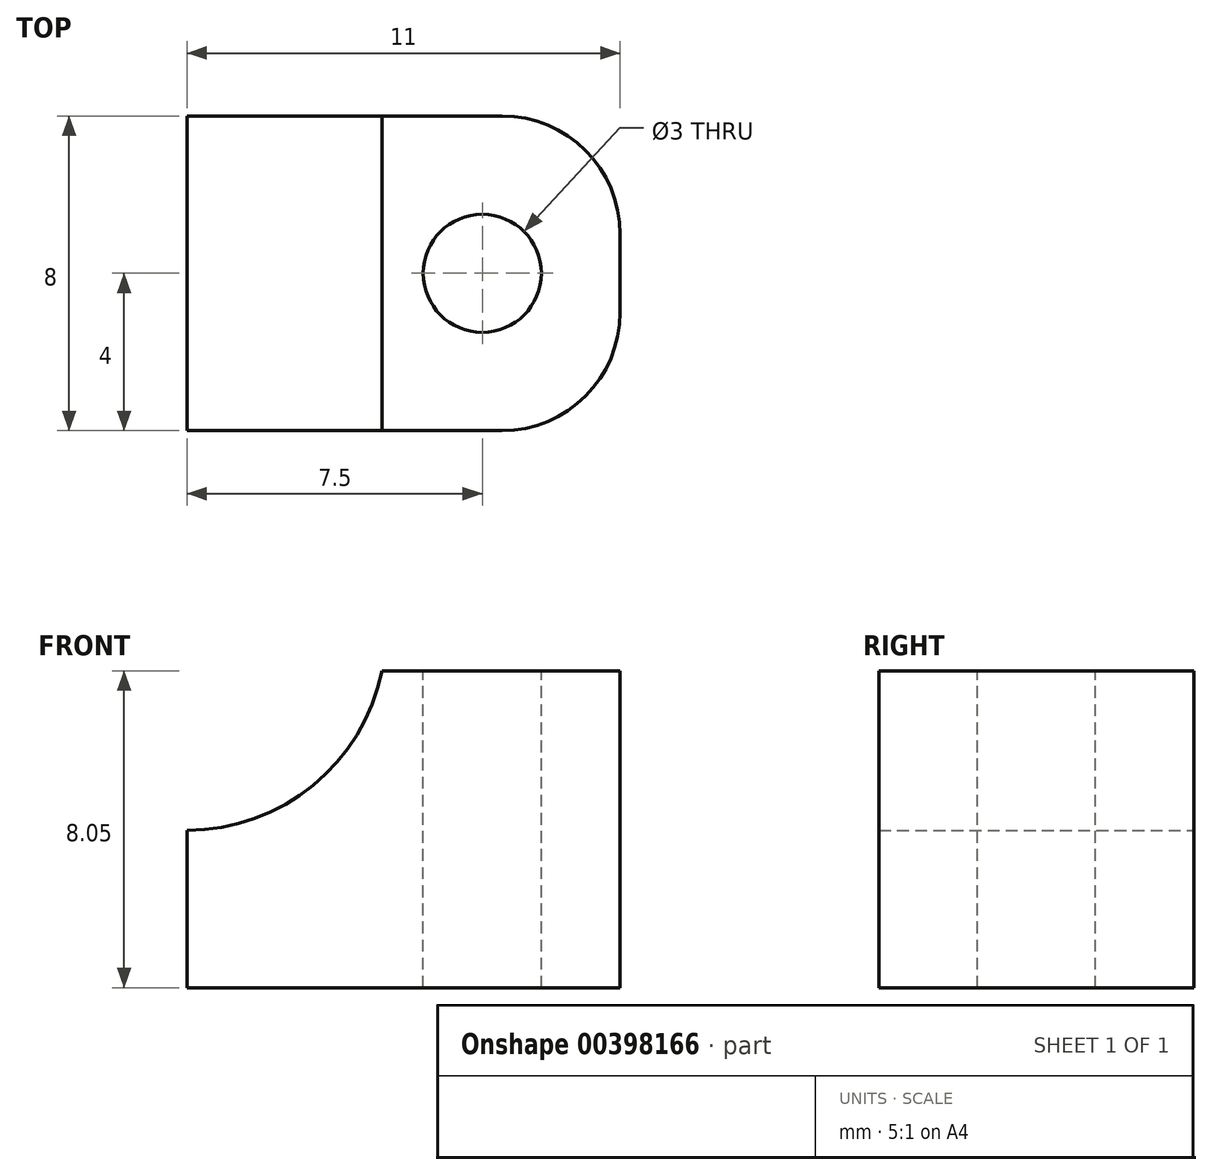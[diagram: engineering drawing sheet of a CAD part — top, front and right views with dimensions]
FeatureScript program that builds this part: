
annotation { "Feature Type Name" : "Feature", "Feature Type Description" : "" }
export const myFeature = defineFeature(function(context is Context, id is Id, definition is map)
    precondition{}
    {
        {
            var Q0;
            Q0=qCreatedBy(makeId("Front.planeOp"),FACE);
            var sketch = newSketch(context, id + "F0", { "sketchPlane" : qUnion([Q0])});
            skLineSegment(sketch, "E0", {"start": v(11, 8.05) * mm, "end": v(11, 0) * mm});
            skLineSegment(sketch, "E1", {"start": v(11, 0) * mm, "end": v(0, 0) * mm});
            skArc(sketch, "E2", {"start": v(0, 4) * mm, "mid": v(3.2, 5.14) * mm, "end": v(4.95, 8.05) * mm});
            skLineSegment(sketch, "E3", {"start": v(0, 4) * mm, "end": v(0, 0) * mm});
            skLineSegment(sketch, "E4", {"start": v(4.95, 8.05) * mm, "end": v(11, 8.05) * mm});
            skPoint(sketch, "E5.orphan", {"position": v(0, 8.05) * mm});
            skSolve(sketch);
        }
        {
            var Q0;
            Q0 = qSketchRegion(id + "F0", true);
            extrude(context, id + "F1", {"entities" : qUnion([Q0]), "depth" : 8 * mm});
        }
        {
            var Q0;
            Q0=makeQuery(id+"F1.opExtrude","SWEPT_FACE",FACE,{"disambiguationData":[OSD([sQuery(id+"F0.wireOp",EDGE,"E4")])]});
            var sketch = newSketch(context, id + "F2", { "sketchPlane" : qUnion([Q0])});
            skCircle(sketch, "E6", {"center": v(7.5, -4) * mm, "radius": 1.5 * mm});
            skLineSegment(sketch, "E7", {"start": v(0, 0) * mm, "end": v(0, -8) * mm});
            skLineSegment(sketch, "E8", {"start": v(0, -4) * mm, "end": v(11, -4) * mm, "construction": true});
            skSolve(sketch);
        }
        {
            var Q0;
            Q0 = qSketchRegion(id + "F2", true);
            extrude(context, id + "F3", {"entities" : qUnion([Q0]), "operationType" : NewBodyOperationType.REMOVE, "oppositeDirection" : true, "depth" : 25 * mm});
        }
        {
            var Q0;
            Q0=makeQuery(id+"F1.opExtrude","CAP_EDGE",EDGE,{"disambiguationData":[OSD([sQuery(id+"F0.wireOp",EDGE,"E0")])],"isStart":true});
            var Q1;
            Q1=makeQuery(id+"F1.opExtrude","CAP_EDGE",EDGE,{"disambiguationData":[OSD([sQuery(id+"F0.wireOp",EDGE,"E0")])],"isStart":false});
            var Q2;
            Q2=makeQuery(id+"F2JzCnKswk5KWSn_1.1.F1.opExtrude","CAP_EDGE",EDGE,{"disambiguationData":[OSD([sQuery(id+"F0.wireOp",EDGE,"E0")])],"isStart":true});
            var Q3;
            Q3=makeQuery(id+"F2JzCnKswk5KWSn_1.1.F1.opExtrude","CAP_EDGE",EDGE,{"disambiguationData":[OSD([sQuery(id+"F0.wireOp",EDGE,"E0")])],"isStart":false});
            fillet(context, id + "F4", {"entities" : qUnion([Q0, Q1, Q2, Q3]), "radius" : 3 * mm, "tangentPropagation" : true, "allowEdgeOverflow" : false});
        }
    });
